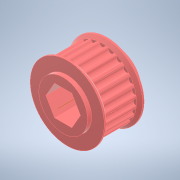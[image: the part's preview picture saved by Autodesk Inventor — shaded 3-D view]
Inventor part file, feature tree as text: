
AUTODESK INVENTOR PART (.ipt)
format: ipt  version: 2022.3 (Build 263350000, 350)  size: 330,752 bytes
history: native  units: in
note: dims shown in document units (in); Inventor stores cm internally (conversion verified against a paired STEP export)
features: extrude x8, sketch x7, mirror x2, chamfer x2, other x1, fillet x1, pattern_circular x1, projected_geometry x1
ambient origin geometry x8: Origin, YZ Plane, XZ Plane, XY Plane, X Axis, Y Axis, Z Axis, Center Point
bodies: Solid1 (feature_tree)
feature tree (23):
  other  "Hex Bore"
  extrude  "HTD Base"  Depth=0.3937in TaperAngle=0.0deg
  extrude  "HTD Flange"  Depth=0.0591in
  mirror  "HTD Flanges"
  chamfer  "HTD Flange Chamfer"  Distance=0.0787in Angle=45.0deg
  extrude  "GT2 Base"  TaperAngle=0.0deg  [1 undecoded]
  extrude  "GT2 Base Tooth"  TaperAngle=0.0deg  [1 undecoded]
  fillet  "GT2 Base Tooth pt. 2"  Radius=0.8723in
  pattern_circular  "GT2 Teeth"  [2 undecoded]
  extrude  "GT2 Flange"  Depth=0.5638in
  mirror  "GT2 Flanges"
  chamfer  "GT2 Flange Chamfer"  Distance=0.0075in
  extrude  "Circle Bore"  TaperAngle=0.0deg  [1 undecoded]
  sketch  "Sketch9"  dims[d25=0.3937in d26=0.0in d27=0.0727in d28=0.0075in d29=0.0in d30=0.0in d31=0.0118in d32=9.4488in d33=360.0deg d35=0.0394in d36=0.0591in d37=0.0in d38=0.0394in d39=0.0787in d40=45.0deg d41=0.625in d42=0.125in d43=0.0in d44=0.5638in d45=0.0in]
  extrude  "Extrusion10"  Depth=0.0118in
  extrude  "Extrusion9"  Depth=0.5638in
  sketch  "Sketch1"  dims[d0=1.4588in d1=0.3937in d2=0.0in]
  sketch  "Sketch4"  dims[d12=0.0394in d13=0.0591in]
  sketch  "Sketch5"  dims[d14=0.0in]
  sketch  "Sketch6"  dims[d15=0.0394in d16=0.0787in d17=45.0deg]
  sketch  "Sketch7"  dims[d18=0.385in d19=0.0in d20=0.0in]
  sketch  "Sketch8"  dims[d21=0.385in d22=0.0in d23=0.0in d24=0.8723in]
  projected_geometry  "Projected Loop1"
note: 5 required parameter values undecoded (feature->parameter linkage not recoverable at this tier; creation-order binding heuristic only, values carry confidence <= 0.55)
